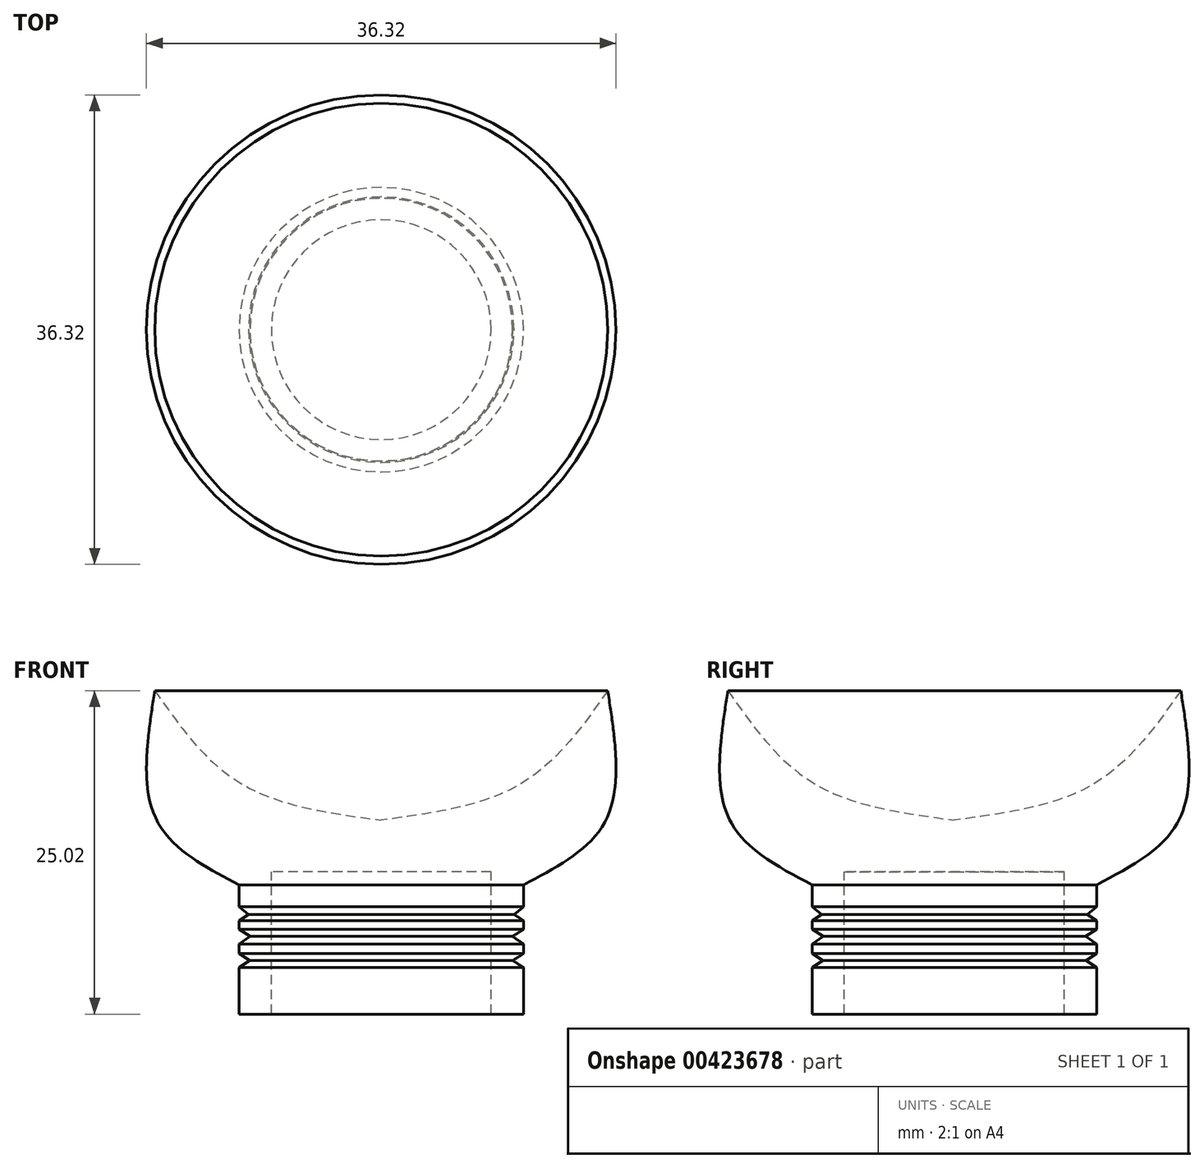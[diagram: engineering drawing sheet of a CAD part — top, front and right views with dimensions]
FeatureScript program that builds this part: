
annotation { "Feature Type Name" : "Feature", "Feature Type Description" : "" }
export const myFeature = defineFeature(function(context is Context, id is Id, definition is map)
    precondition{}
    {
        {
            var Q0;
            Q0=qCreatedBy(makeId("Front.planeOp"),FACE);
            var sketch = newSketch(context, id + "F0", { "sketchPlane" : qUnion([Q0])});
            skLineSegment(sketch, "E0", {"start": v(-8.5, 0) * mm, "end": v(-11, 0) * mm});
            skLineSegment(sketch, "E1", {"start": v(-11, 0) * mm, "end": v(-11, 3.61) * mm});
            skFitSpline(sketch, "E2", {"points": [v(-11, 10) * mm, v(-17.4, 15.08) * mm, v(-17.52, 25.02) * mm], "startDerivative": vector(-16.62, 8.7) * mm, "endDerivative": vector(3.27, 21.12) * mm});
            skFitSpline(sketch, "E3", {"points": [v(-17.52, 25.02) * mm, v(-10.87, 17.84) * mm, v(0, 15) * mm], "startDerivative": vector(12.02, -17.13) * mm, "endDerivative": vector(22.88, -3.07) * mm});
            skLineSegment(sketch, "E4", {"start": v(0, 15) * mm, "end": v(0, 0) * mm});
            skLineSegment(sketch, "E5", {"start": v(-18.07, 20.81) * mm, "end": v(-17.47, 20.29) * mm});
            skLineSegment(sketch, "E6", {"start": v(-17.47, 20.29) * mm, "end": v(-18.13, 20.04) * mm});
            skLineSegment(sketch, "E7", {"start": v(-18.15, 19.55) * mm, "end": v(-17.53, 19.18) * mm});
            skLineSegment(sketch, "E8", {"start": v(-17.53, 19.18) * mm, "end": v(-18.15, 18.67) * mm});
            skLineSegment(sketch, "E9", {"start": v(-18.14, 18.27) * mm, "end": v(-17.52, 17.98) * mm});
            skLineSegment(sketch, "E10", {"start": v(-17.52, 17.98) * mm, "end": v(-18.07, 17.43) * mm});
            skLineSegment(sketch, "E11", {"start": v(-18.14, 18.27) * mm, "end": v(-18.15, 18.67) * mm});
            skLineSegment(sketch, "E12", {"start": v(-8.5, 0) * mm, "end": v(-8.5, 11) * mm});
            skLineSegment(sketch, "E13", {"start": v(-8.5, 11) * mm, "end": v(0, 11) * mm});
            skLineSegment(sketch, "E14", {"start": v(-11, 8.3) * mm, "end": v(-10.27, 7.7) * mm});
            skLineSegment(sketch, "E15", {"start": v(-10.27, 7.7) * mm, "end": v(-11, 7.23) * mm});
            skLineSegment(sketch, "E16", {"start": v(-11, 6.55) * mm, "end": v(-10.15, 6.01) * mm});
            skLineSegment(sketch, "E17", {"start": v(-10.15, 6.01) * mm, "end": v(-11, 5.42) * mm});
            skLineSegment(sketch, "E18", {"start": v(-11, 5.42) * mm, "end": v(-11, 4.68) * mm});
            skLineSegment(sketch, "E19", {"start": v(-11, 4.68) * mm, "end": v(-10.18, 4.14) * mm});
            skLineSegment(sketch, "E20", {"start": v(-10.18, 4.14) * mm, "end": v(-11, 3.61) * mm});
            skLineSegment(sketch, "E21.trimOffspring", {"start": v(-11, 4.68) * mm, "end": v(-11, 5.42) * mm});
            skLineSegment(sketch, "E22.trimOffspring", {"start": v(-11, 6.55) * mm, "end": v(-11, 7.23) * mm});
            skLineSegment(sketch, "E23.trimOffspring", {"start": v(-11, 8.3) * mm, "end": v(-11, 10) * mm});
            skSolve(sketch);
        }
        {
            var Q0;
            Q0 = qSketchRegion(id + "F0", true);
            var Q1;
            Q1=sQuery(id+"F0.wireOp",EDGE,"E4");
            revolve(context, id + "F1", {"entities" : qUnion([Q0]), "axis" : qUnion([Q1]), "revolveType" : RevolveType.FULL});
        }
    });
